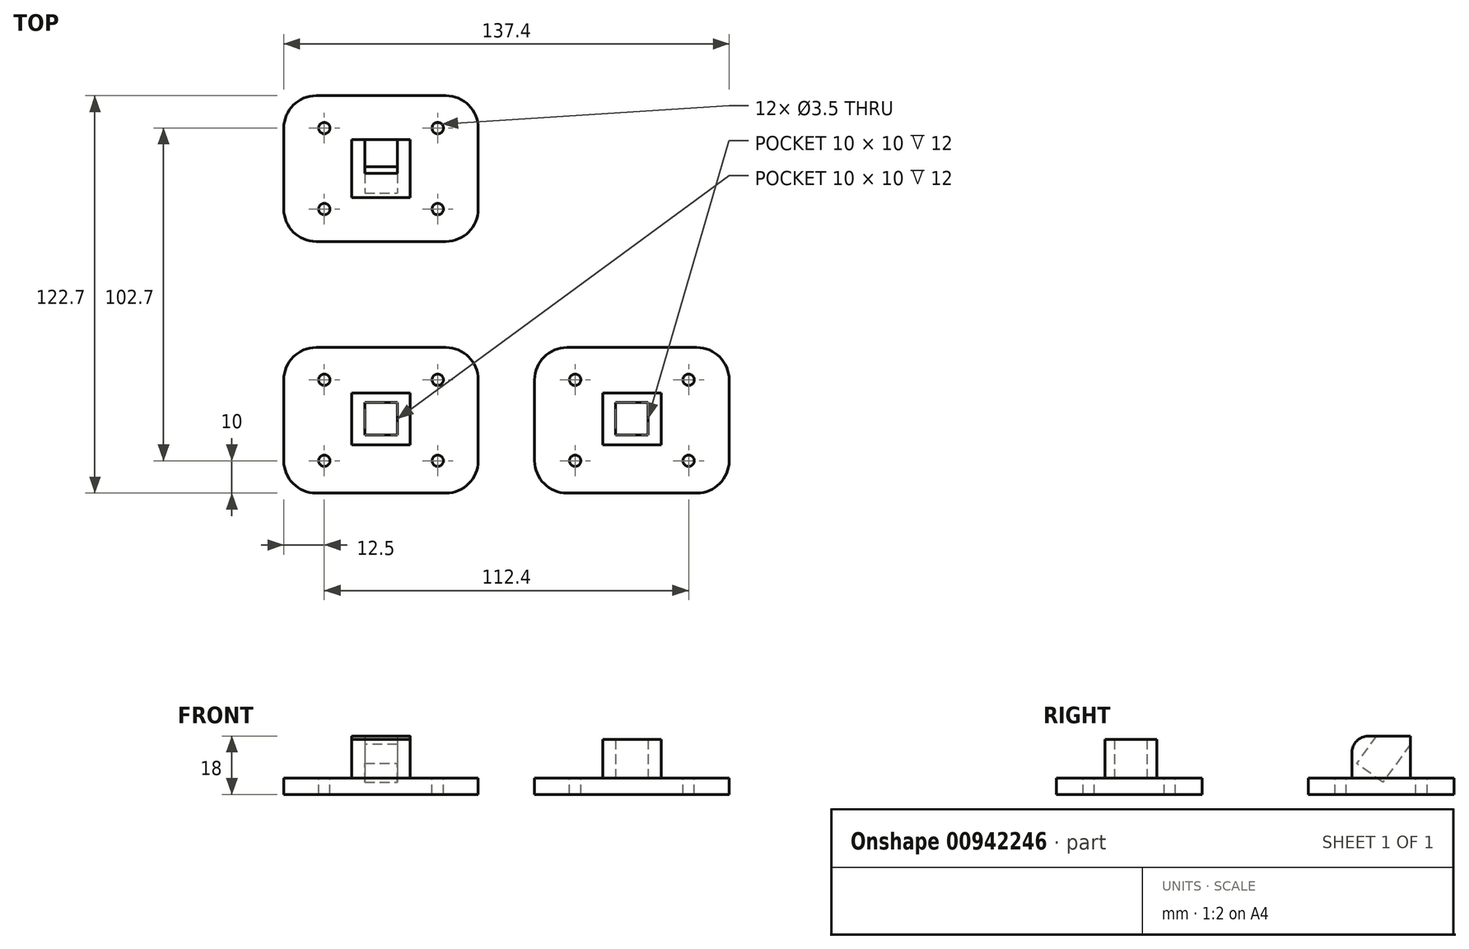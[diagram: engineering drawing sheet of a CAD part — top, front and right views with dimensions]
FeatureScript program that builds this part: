
annotation { "Feature Type Name" : "Feature", "Feature Type Description" : "" }
export const myFeature = defineFeature(function(context is Context, id is Id, definition is map)
    precondition{}
    {
        {
            var Q0;
            Q0=qCreatedBy(makeId("Top.planeOp"),FACE);
            var sketch = newSketch(context, id + "F0", { "sketchPlane" : qUnion([Q0])});
            skLineSegment(sketch, "E0.bottom", {"start": v(20, 22.5) * mm, "end": v(-20, 22.5) * mm});
            skLineSegment(sketch, "E0.top", {"start": v(20, -22.5) * mm, "end": v(-20, -22.5) * mm});
            skLineSegment(sketch, "E0.left", {"start": v(30, 12.5) * mm, "end": v(30, -12.5) * mm});
            skLineSegment(sketch, "E0.right", {"start": v(-30, 12.5) * mm, "end": v(-30, -12.5) * mm});
            skPoint(sketch, "E0.middle", {"position": v(0, 0) * mm});
            skPoint(sketch, "E1.visualSharp", {"position": v(30, -22.5) * mm});
            skArc(sketch, "E1.filletArc", {"start": v(20, -22.5) * mm, "mid": v(27.07, -19.57) * mm, "end": v(30, -12.5) * mm});
            skPoint(sketch, "E2.visualSharp", {"position": v(-30, -22.5) * mm});
            skArc(sketch, "E2.filletArc", {"start": v(-30, -12.5) * mm, "mid": v(-27.07, -19.57) * mm, "end": v(-20, -22.5) * mm});
            skPoint(sketch, "E3.visualSharp", {"position": v(-30, 22.5) * mm});
            skArc(sketch, "E3.filletArc", {"start": v(-20, 22.5) * mm, "mid": v(-27.07, 19.57) * mm, "end": v(-30, 12.5) * mm});
            skPoint(sketch, "E4.visualSharp", {"position": v(30, 22.5) * mm});
            skArc(sketch, "E4.filletArc", {"start": v(30, 12.5) * mm, "mid": v(27.07, 19.57) * mm, "end": v(20, 22.5) * mm});
            skSolve(sketch);
        }
        {
            var Q0;
            Q0=makeQuery(id+"F0.imprint","IMPRINT",FACE,{"disambiguationData":[TD([[makeQuery(id+"F0.imprint","IMPRINT",EDGE,{"derivedFrom":sQuery(id+"F0.wireOp",EDGE,"E0.bottom")}),1.0]])]});
            extrude(context, id + "F1", {"entities" : qUnion([Q0]), "depth" : 5 * mm, "offsetDistance" : 25 * mm});
        }
        {
            var Q0;
            Q0=makeQuery(id+"F1.opExtrude","CAP_FACE",FACE,{"disambiguationData":[OSD([sQuery(id+"F0.wireOp",EDGE,"E0.bottom"),sQuery(id+"F0.wireOp",EDGE,"E0.top"),sQuery(id+"F0.wireOp",EDGE,"E0.left"),sQuery(id+"F0.wireOp",EDGE,"E0.right"),sQuery(id+"F0.wireOp",EDGE,"E1.filletArc"),sQuery(id+"F0.wireOp",EDGE,"E2.filletArc"),sQuery(id+"F0.wireOp",EDGE,"E3.filletArc"),sQuery(id+"F0.wireOp",EDGE,"E4.filletArc")])],"isStart":false});
            var sketch = newSketch(context, id + "F2", { "sketchPlane" : qUnion([Q0])});
            skCircle(sketch, "E5", {"center": v(17.5, -12.5) * mm, "radius": 1.75 * mm});
            skCircle(sketch, "E6", {"center": v(-17.5, -12.5) * mm, "radius": 1.75 * mm});
            skCircle(sketch, "E7", {"center": v(-17.5, 12.5) * mm, "radius": 1.75 * mm});
            skCircle(sketch, "E8", {"center": v(17.5, 12.5) * mm, "radius": 1.75 * mm});
            skSolve(sketch);
        }
        {
            var Q0;
            Q0=makeQuery(id+"F2.imprint","IMPRINT",FACE,{"disambiguationData":[TD([[makeQuery(id+"F2.imprint","IMPRINT",EDGE,{"derivedFrom":sQuery(id+"F2.wireOp",EDGE,"E8")}),1.0]])]});
            var Q1;
            Q1=makeQuery(id+"F2.imprint","IMPRINT",FACE,{"disambiguationData":[TD([[makeQuery(id+"F2.imprint","IMPRINT",EDGE,{"derivedFrom":sQuery(id+"F2.wireOp",EDGE,"E5")}),1.0]])]});
            var Q2;
            Q2=makeQuery(id+"F2.imprint","IMPRINT",FACE,{"disambiguationData":[TD([[makeQuery(id+"F2.imprint","IMPRINT",EDGE,{"derivedFrom":sQuery(id+"F2.wireOp",EDGE,"E6")}),1.0]])]});
            var Q3;
            Q3=makeQuery(id+"F2.imprint","IMPRINT",FACE,{"disambiguationData":[TD([[makeQuery(id+"F2.imprint","IMPRINT",EDGE,{"derivedFrom":sQuery(id+"F2.wireOp",EDGE,"E7")}),1.0]])]});
            extrude(context, id + "F3", {"entities" : qUnion([Q0, Q1, Q2, Q3]), "operationType" : NewBodyOperationType.REMOVE, "oppositeDirection" : true, "depth" : 25 * mm, "offsetDistance" : 25 * mm});
        }
        {
            var Q0;
            Q0=makeQuery(id+"F1.opExtrude","CAP_FACE",FACE,{"disambiguationData":[OSD([sQuery(id+"F0.wireOp",EDGE,"E0.bottom"),sQuery(id+"F0.wireOp",EDGE,"E0.top"),sQuery(id+"F0.wireOp",EDGE,"E0.left"),sQuery(id+"F0.wireOp",EDGE,"E0.right"),sQuery(id+"F0.wireOp",EDGE,"E1.filletArc"),sQuery(id+"F0.wireOp",EDGE,"E2.filletArc"),sQuery(id+"F0.wireOp",EDGE,"E3.filletArc"),sQuery(id+"F0.wireOp",EDGE,"E4.filletArc")])],"isStart":false});
            var sketch = newSketch(context, id + "F4", { "sketchPlane" : qUnion([Q0])});
            skLineSegment(sketch, "E9.bottom", {"start": v(-9, 8.45) * mm, "end": v(9, 8.45) * mm});
            skLineSegment(sketch, "E9.top", {"start": v(-9, -7.55) * mm, "end": v(9, -7.55) * mm});
            skLineSegment(sketch, "E9.left", {"start": v(-9, 8.45) * mm, "end": v(-9, -7.55) * mm});
            skLineSegment(sketch, "E9.right", {"start": v(9, 8.45) * mm, "end": v(9, -7.55) * mm});
            skPoint(sketch, "E9.middle", {"position": v(0, 0.45) * mm});
            skLineSegment(sketch, "E10.bottom", {"start": v(-5, -4.55) * mm, "end": v(5, -4.55) * mm});
            skLineSegment(sketch, "E10.top", {"start": v(-5, 5.45) * mm, "end": v(5, 5.45) * mm});
            skLineSegment(sketch, "E10.left", {"start": v(-5, -4.55) * mm, "end": v(-5, 5.45) * mm});
            skLineSegment(sketch, "E10.right", {"start": v(5, -4.55) * mm, "end": v(5, 5.45) * mm});
            skSolve(sketch);
        }
        {
            var Q0;
            Q0=makeQuery(id+"F4.imprint","IMPRINT",FACE,{"disambiguationData":[TD([[makeQuery(id+"F4.imprint","IMPRINT",EDGE,{"derivedFrom":sQuery(id+"F4.wireOp",EDGE,"E9.bottom")}),-1.0]])]});
            extrude(context, id + "F5", {"entities" : qUnion([Q0]), "operationType" : NewBodyOperationType.ADD, "depth" : 12 * mm, "offsetDistance" : 25 * mm});
        }
        {
            var Q0;
            Q0=makeQuery(id+"F1.opExtrude","SWEPT_BODY",BODY,{"disambiguationData":[OSD([sQuery(id+"F0.wireOp",EDGE,"E0.bottom"),sQuery(id+"F0.wireOp",EDGE,"E0.top"),sQuery(id+"F0.wireOp",EDGE,"E0.left"),sQuery(id+"F0.wireOp",EDGE,"E0.right"),sQuery(id+"F0.wireOp",EDGE,"E1.filletArc"),sQuery(id+"F0.wireOp",EDGE,"E2.filletArc"),sQuery(id+"F0.wireOp",EDGE,"E3.filletArc"),sQuery(id+"F0.wireOp",EDGE,"E4.filletArc")])]});
            transform(context, id + "F6", {"entities" : qUnion([Q0]), "transformType" : TransformType.TRANSLATION_3D, "dx" : 77.4 * mm, "dy" : 0 * mm, "dz" : 0 * mm, "makeCopy" : true});
        }
        {
            var Q0;
            Q0=makeQuery(id+"F1.opExtrude","SWEPT_BODY",BODY,{"disambiguationData":[OSD([sQuery(id+"F0.wireOp",EDGE,"E0.bottom"),sQuery(id+"F0.wireOp",EDGE,"E0.top"),sQuery(id+"F0.wireOp",EDGE,"E0.left"),sQuery(id+"F0.wireOp",EDGE,"E0.right"),sQuery(id+"F0.wireOp",EDGE,"E1.filletArc"),sQuery(id+"F0.wireOp",EDGE,"E2.filletArc"),sQuery(id+"F0.wireOp",EDGE,"E3.filletArc"),sQuery(id+"F0.wireOp",EDGE,"E4.filletArc")])]});
            transform(context, id + "F7", {"entities" : qUnion([Q0]), "transformType" : TransformType.TRANSLATION_3D, "dx" : 0 * mm, "dy" : 77.7 * mm, "dz" : 0 * mm, "makeCopy" : true});
        }
        {
            var Q0;
            Q0=makeQuery(id+"F7.opPattern","COPY",FACE,{"derivedFrom":makeQuery(id+"F5.opExtrude","CAP_FACE",FACE,{"disambiguationData":[OSD([sQuery(id+"F4.wireOp",EDGE,"E9.bottom"),sQuery(id+"F4.wireOp",EDGE,"E9.top"),sQuery(id+"F4.wireOp",EDGE,"E9.left"),sQuery(id+"F4.wireOp",EDGE,"E9.right"),sQuery(id+"F4.wireOp",EDGE,"E10.bottom"),sQuery(id+"F4.wireOp",EDGE,"E10.top"),sQuery(id+"F4.wireOp",EDGE,"E10.left"),sQuery(id+"F4.wireOp",EDGE,"E10.right")])],"isStart":false}),"instanceName":"1"});
            extrude(context, id + "F8", {"entities" : qUnion([Q0]), "operationType" : NewBodyOperationType.REMOVE, "oppositeDirection" : true, "depth" : 12 * mm, "offsetDistance" : 25 * mm});
        }
        {
            var Q0;
            {var subQ0=sQuery(id+"F4.wireOp",EDGE,"E10.right");var subQ1=sQuery(id+"F4.wireOp",EDGE,"E10.left");var subQ2=sQuery(id+"F4.wireOp",EDGE,"E10.top");var subQ3=sQuery(id+"F4.wireOp",EDGE,"E10.bottom");var subQ4=sQuery(id+"F4.wireOp",EDGE,"E9.right");var subQ5=sQuery(id+"F4.wireOp",EDGE,"E9.left");var subQ6=sQuery(id+"F4.wireOp",EDGE,"E9.top");var subQ7=sQuery(id+"F4.wireOp",EDGE,"E9.bottom");var subQ8=sQuery(id+"F0.wireOp",EDGE,"E4.filletArc");var subQ9=sQuery(id+"F0.wireOp",EDGE,"E3.filletArc");var subQ10=sQuery(id+"F0.wireOp",EDGE,"E2.filletArc");var subQ11=sQuery(id+"F0.wireOp",EDGE,"E1.filletArc");var subQ12=sQuery(id+"F0.wireOp",EDGE,"E0.right");var subQ13=sQuery(id+"F0.wireOp",EDGE,"E0.left");var subQ14=sQuery(id+"F0.wireOp",EDGE,"E0.top");var subQ15=sQuery(id+"F0.wireOp",EDGE,"E0.bottom");var subQ16=makeQuery(id+"F1.opExtrude","CAP_FACE",FACE,{"disambiguationData":[OSD([subQ15,subQ14,subQ13,subQ12,subQ11,subQ10,subQ9,subQ8])],"isStart":false});Q0=makeQuery(id+"F8.boolean.opBoolean","MERGE",FACE,{"derivedFrom":[makeQuery(id+"F7.opPattern","COPY",FACE,{"derivedFrom":makeQuery(id+"F5.boolean.opBoolean","SPLIT",FACE,{"disambiguationData":[TD([makeQuery(id+"F1.opExtrude","SWEPT_FACE",FACE,{"disambiguationData":[OSD([subQ15])]})])],"derivedFrom":subQ16}),"instanceName":"1"}),makeQuery(id+"F7.opPattern","COPY",FACE,{"derivedFrom":makeQuery(id+"F5.boolean.opBoolean","SPLIT",FACE,{"disambiguationData":[TD([makeQuery(id+"F5.opExtrude","SWEPT_FACE",FACE,{"disambiguationData":[OSD([subQ3])]})])],"derivedFrom":subQ16}),"instanceName":"1"})],"fromTools":[makeQuery(id+"F8.opExtrude","CAP_FACE",FACE,{"disambiguationData":[OSD([subQ7,subQ6,subQ5,subQ4,subQ3,subQ2,subQ1,subQ0])],"isStart":false})]});}
            var sketch = newSketch(context, id + "F9", { "sketchPlane" : qUnion([Q0])});
            skLineSegment(sketch, "E11.bottom", {"start": v(-9, 86.7) * mm, "end": v(9, 86.7) * mm});
            skLineSegment(sketch, "E11.top", {"start": v(-9, 68.7) * mm, "end": v(9, 68.7) * mm});
            skLineSegment(sketch, "E11.left", {"start": v(-9, 86.7) * mm, "end": v(-9, 68.7) * mm});
            skLineSegment(sketch, "E11.right", {"start": v(9, 86.7) * mm, "end": v(9, 68.7) * mm});
            skPoint(sketch, "E11.middle", {"position": v(0, 77.7) * mm});
            skSolve(sketch);
        }
        {
            var Q0;
            Q0=makeQuery(id+"F9.imprint","IMPRINT",FACE,{"disambiguationData":[TD([[makeQuery(id+"F9.imprint","IMPRINT",EDGE,{"derivedFrom":sQuery(id+"F9.wireOp",EDGE,"E11.bottom")}),-1.0]])]});
            extrude(context, id + "F10", {"entities" : qUnion([Q0]), "operationType" : NewBodyOperationType.ADD, "depth" : 13 * mm, "offsetDistance" : 25 * mm});
        }
        {
            var Q0;
            Q0=makeQuery(id+"F10.opExtrude","CAP_VERTEX",VERTEX,{"disambiguationData":[OSD([sQuery(id+"F9.wireOp",EDGE,"E11.bottom"),sQuery(id+"F9.wireOp",EDGE,"E11.left")])],"isStart":true});
            var Q1;
            Q1=makeQuery(id+"F10.opExtrude","CAP_VERTEX",VERTEX,{"disambiguationData":[OSD([sQuery(id+"F9.wireOp",EDGE,"E11.bottom"),sQuery(id+"F9.wireOp",EDGE,"E11.right")])],"isStart":true});
            var Q2;
            Q2=makeQuery(id+"F10.opExtrude","CAP_VERTEX",VERTEX,{"disambiguationData":[OSD([sQuery(id+"F9.wireOp",EDGE,"E11.top"),sQuery(id+"F9.wireOp",EDGE,"E11.left")])],"isStart":false});
            cPlane(context, id + "F11", {"entities" : qUnion([Q0, Q1, Q2]), "cplaneType" : CPlaneType.THREE_POINT, "offset" : 25 * mm, "width" : 150 * mm, "height" : 150 * mm});
        }
        {
            var Q0;
            Q0=qCreatedBy(id+"F11.planeOp",FACE);
            var sketch = newSketch(context, id + "F12", { "sketchPlane" : qUnion([Q0])});
            skLineSegment(sketch, "E12.bottom", {"start": v(-5, 61.24) * mm, "end": v(5, 61.24) * mm});
            skLineSegment(sketch, "E12.top", {"start": v(-5, 51.24) * mm, "end": v(5, 51.24) * mm});
            skLineSegment(sketch, "E12.left", {"start": v(-5, 61.24) * mm, "end": v(-5, 51.24) * mm});
            skLineSegment(sketch, "E12.right", {"start": v(5, 61.24) * mm, "end": v(5, 51.24) * mm});
            skPoint(sketch, "E12.middle", {"position": v(0, 56.24) * mm});
            skPoint(sketch, "E13.left.start.orphan", {"position": v(-2.12, 59.75) * mm});
            skPoint(sketch, "E13.right.start.orphan", {"position": v(2.12, 57.57) * mm});
            skPoint(sketch, "E13.top.end.orphan", {"position": v(2.12, 52.72) * mm});
            skPoint(sketch, "E13.top.start.orphan", {"position": v(-2.12, 54.9) * mm});
            skSolve(sketch);
        }
        {
            var Q0;
            Q0 = qSketchRegion(id + "F12", true);
            extrude(context, id + "F13", {"entities" : qUnion([Q0]), "operationType" : NewBodyOperationType.REMOVE, "depth" : 25 * mm, "offsetDistance" : 25 * mm, "hasSecondDirection" : true, "secondDirectionOppositeDirection" : true, "secondDirectionDepth" : 6 * mm});
        }
        {
            var Q0;
            Q0=makeQuery(id+"F10.opExtrude","CAP_EDGE",EDGE,{"disambiguationData":[OSD([sQuery(id+"F9.wireOp",EDGE,"E11.top")])],"isStart":false});
            fillet(context, id + "F14", {"entities" : qUnion([Q0]), "radius" : 5 * mm, "tangentPropagation" : true, "allowEdgeOverflow" : false});
        }
    });
